# Revit family: KEUCO_11573170000
name_source: partatom
category: Allgemeines Modell
revit_build: Autodesk Revit 2016 (Build: 20150220_1215(x64)
units: mm (PartAtom-declared; Revit-internal decimal feet)

## family parameters
Arbeitsebenenbasiert = Ja
Beim Laden mit Abzugskörper schneiden = Nein
Bemaßung runder Anschluss = Durchmesser verwenden
Gemeinsam genutzt = Nein
Immer vertikal = Nein
Kann Basisbauteil für Bewehrung sein = Nein
Raumberechnungspunkt = Nein
Teiletyp = Normal

## types (1)
- 11573170000
    Artikelnummer = 11573170000
    Ausschreibungstext = KEUCO Edition 400 Toilettenpapierhalter mit Ablage, 11573170000
Toilettenpapierhalter  aus massivem Aluminium, für Rollenbreite 100/120mm, 
mit Ablagemöglichkeit, z.B. für  Handys und Accessoires,
silber-eloxiert (E6 EV1), Wandmodell, mit leicht gerundeten Kanten,
Breite 328 mm, Stärke 10 mm, Tiefe 100 mm, Ablagefläche 185 mm breit
der Toilettenpapierhalter mit Ablage wird verdeckt angebracht,
Lieferung inkl. korrosionsfreiem Befestigungsmaterial
    Beschreibung = mit Ablage, offene Form
für Rollenbreite 100/120 mm
    Gewicht = 806
    Hersteller = KEUCO
    Kategorie = ACC
    Serie = Plan
    Stange Material = Aluminium
    URL = https://www.keuco.com
    Verwendung = GWC / WC
    Vorgabe-Ansicht = 1219 mm

## geometry (parser evidence)
native form markers: Blend x9, Sweep x3
no freeform markers — native parametric forms only
